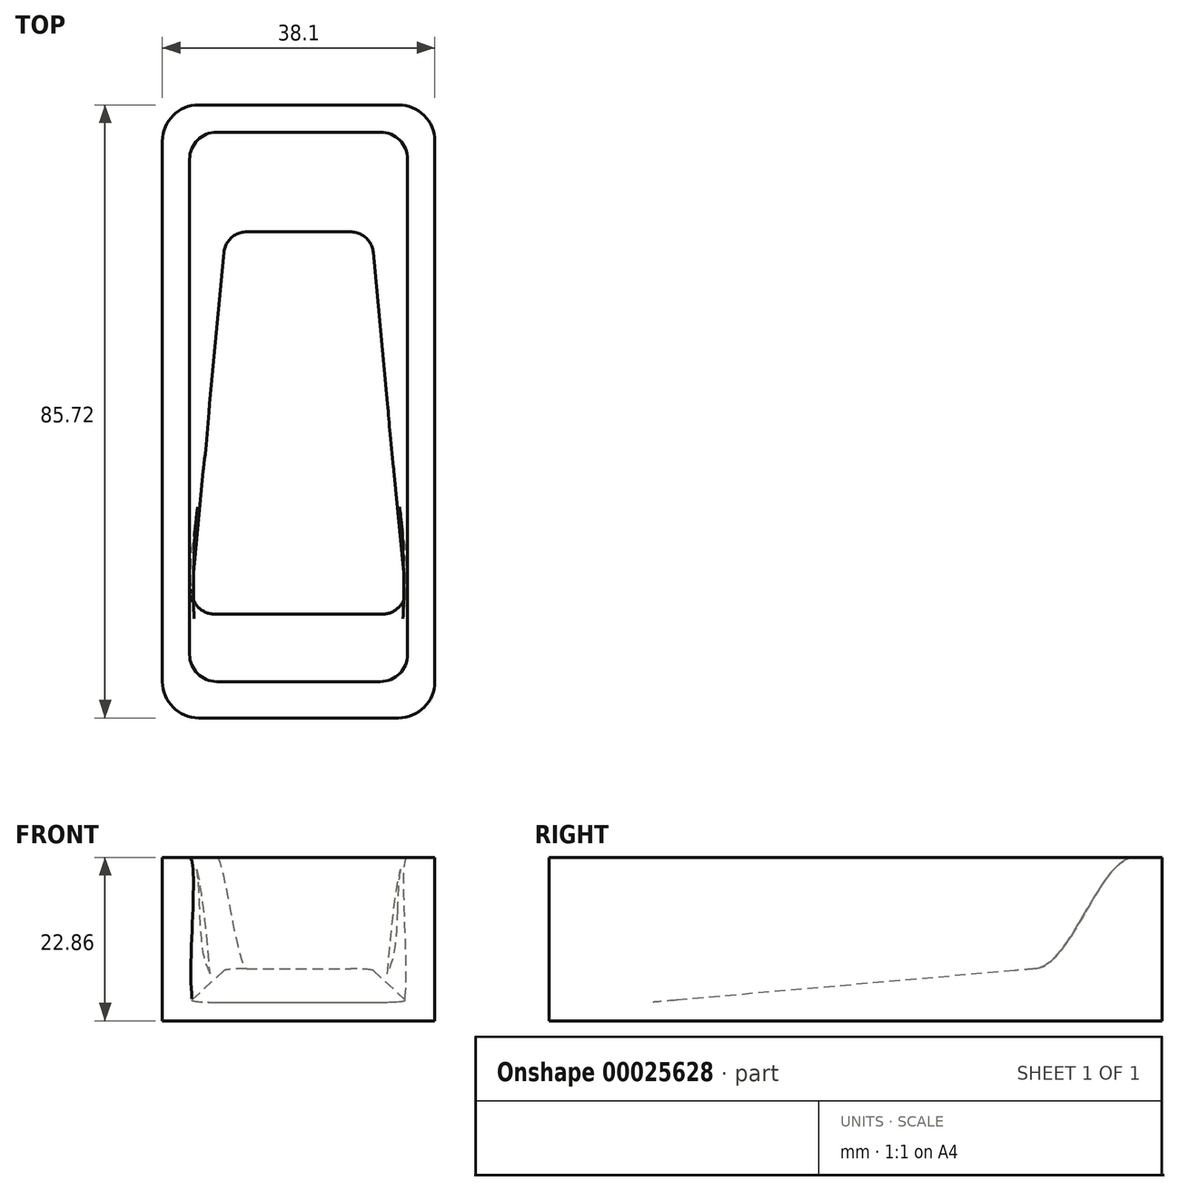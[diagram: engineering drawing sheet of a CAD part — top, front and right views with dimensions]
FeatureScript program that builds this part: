
annotation { "Feature Type Name" : "Feature", "Feature Type Description" : "" }
export const myFeature = defineFeature(function(context is Context, id is Id, definition is map)
    precondition{}
    {
        {
            var Q0;
            Q0=qCreatedBy(makeId("Top.planeOp"),FACE);
            var sketch = newSketch(context, id + "F0", { "sketchPlane" : qUnion([Q0])});
            skLineSegment(sketch, "E0.bottom", {"start": v(-19.05, 42.86) * mm, "end": v(19.05, 42.86) * mm});
            skLineSegment(sketch, "E0.top", {"start": v(-19.05, -42.86) * mm, "end": v(19.05, -42.86) * mm});
            skLineSegment(sketch, "E0.left", {"start": v(-19.05, 42.86) * mm, "end": v(-19.05, -42.86) * mm});
            skLineSegment(sketch, "E0.right", {"start": v(19.05, 42.86) * mm, "end": v(19.05, -42.86) * mm});
            skSolve(sketch);
        }
        {
            var Q0;
            Q0 = qSketchRegion(id + "F0", true);
            extrude(context, id + "F1", {"entities" : qUnion([Q0]), "depth" : 22.86 * mm});
        }
        {
            var Q0;
            Q0=qCreatedBy(makeId("Top.planeOp"),FACE);
            cPlane(context, id + "F2", {"entities" : qUnion([Q0]), "cplaneType" : CPlaneType.OFFSET, "offset" : 5.08 * mm, "width" : 152.4 * mm, "height" : 152.4 * mm});
        }
        {
            var Q0;
            Q0=qCreatedBy(id+"F2.planeOp",FACE);
            var sketch = newSketch(context, id + "F3", { "sketchPlane" : qUnion([Q0])});
            skLineSegment(sketch, "E1", {"start": v(-38.1, 0) * mm, "end": v(38.1, 0) * mm, "construction": true});
            skSolve(sketch);
        }
        {
            var Q0;
            Q0=sQuery(id+"F3.wireOp",EDGE,"E1");
            cPlane(context, id + "F4", {"entities" : qUnion([Q0]), "cplaneType" : CPlaneType.LINE_ANGLE, "offset" : 152.4 * mm, "angle" : 95 * degree, "width" : 152.4 * mm, "height" : 152.4 * mm});
        }
        {
            var Q0;
            Q0=makeQuery(id+"F1.opExtrude","CAP_FACE",FACE,{"disambiguationData":[OSD([sQuery(id+"F0.wireOp",EDGE,"E0.bottom"),sQuery(id+"F0.wireOp",EDGE,"E0.top"),sQuery(id+"F0.wireOp",EDGE,"E0.left"),sQuery(id+"F0.wireOp",EDGE,"E0.right")])],"isStart":false});
            var sketch = newSketch(context, id + "F5", { "sketchPlane" : qUnion([Q0])});
            skLineSegment(sketch, "E2.bottom", {"start": v(-11.43, 39.05) * mm, "end": v(11.43, 39.05) * mm});
            skLineSegment(sketch, "E2.top", {"start": v(-11.43, -37.78) * mm, "end": v(11.43, -37.78) * mm});
            skLineSegment(sketch, "E2.left", {"start": v(-15.24, 35.24) * mm, "end": v(-15.24, -33.97) * mm});
            skLineSegment(sketch, "E2.right", {"start": v(15.24, 35.24) * mm, "end": v(15.24, -33.97) * mm});
            skPoint(sketch, "E3.visualSharp", {"position": v(-15.24, 39.05) * mm});
            skArc(sketch, "E3.filletArc", {"start": v(-11.43, 39.05) * mm, "mid": v(-14.12, 37.94) * mm, "end": v(-15.24, 35.24) * mm});
            skPoint(sketch, "E4.visualSharp", {"position": v(15.24, 39.05) * mm});
            skArc(sketch, "E4.filletArc", {"start": v(15.24, 35.24) * mm, "mid": v(14.12, 37.94) * mm, "end": v(11.43, 39.05) * mm});
            skPoint(sketch, "E5.visualSharp", {"position": v(15.24, -37.78) * mm});
            skArc(sketch, "E5.filletArc", {"start": v(11.43, -37.78) * mm, "mid": v(14.12, -36.67) * mm, "end": v(15.24, -33.97) * mm});
            skPoint(sketch, "E6.visualSharp", {"position": v(-15.24, -37.78) * mm});
            skArc(sketch, "E6.filletArc", {"start": v(-15.24, -33.97) * mm, "mid": v(-14.12, -36.67) * mm, "end": v(-11.43, -37.78) * mm});
            skSolve(sketch);
        }
        {
            var Q0;
            Q0=qCreatedBy(id+"F4.planeOp",FACE);
            var sketch = newSketch(context, id + "F6", { "sketchPlane" : qUnion([Q0])});
            skLineSegment(sketch, "E7.bottom", {"start": v(-7.27, 25.64) * mm, "end": v(7.27, 25.64) * mm});
            skLineSegment(sketch, "E7.top", {"start": v(-11.75, -28) * mm, "end": v(11.75, -28) * mm});
            skLineSegment(sketch, "E7.left", {"start": v(-10.43, 22.77) * mm, "end": v(-14.91, -24.53) * mm});
            skLineSegment(sketch, "E7.right", {"start": v(10.43, 22.77) * mm, "end": v(14.91, -24.53) * mm});
            skPoint(sketch, "E8.visualSharp", {"position": v(-10.16, 25.64) * mm});
            skArc(sketch, "E8.filletArc", {"start": v(-7.27, 25.64) * mm, "mid": v(-9.4, 24.82) * mm, "end": v(-10.43, 22.77) * mm});
            skPoint(sketch, "E9.visualSharp", {"position": v(10.16, 25.64) * mm});
            skArc(sketch, "E9.filletArc", {"start": v(10.43, 22.77) * mm, "mid": v(9.4, 24.82) * mm, "end": v(7.27, 25.64) * mm});
            skPoint(sketch, "E10.visualSharp", {"position": v(15.24, -28) * mm});
            skArc(sketch, "E10.filletArc", {"start": v(11.75, -28) * mm, "mid": v(14.1, -26.97) * mm, "end": v(14.91, -24.53) * mm});
            skPoint(sketch, "E11.visualSharp", {"position": v(-15.24, -28) * mm});
            skArc(sketch, "E11.filletArc", {"start": v(-14.91, -24.53) * mm, "mid": v(-14.1, -26.97) * mm, "end": v(-11.75, -28) * mm});
            skSolve(sketch);
        }
        {
            var Q1;
            Q1 = qSketchRegion(id + "F5", true);
            var Q2;
            Q2 = qSketchRegion(id + "F6", true);
            loft(context, id + "F7", {"operationType" : NewBodyOperationType.REMOVE, "startCondition" : LoftEndDerivativeType.MATCH_TANGENT, "startMagnitude" : 1, "endCondition" : LoftEndDerivativeType.TANGENT_TO_PROFILE, "endMagnitude" : 1, "sheetProfilesArray" : [{ "sheetProfileEntities" : qUnion([Q1]) }, { "sheetProfileEntities" : qUnion([Q2]) }]});
        }
        {
            var Q0;
            Q0=makeQuery(id+"F1.opExtrude","SWEPT_EDGE",EDGE,{"disambiguationData":[OSD([sQuery(id+"F0.wireOp",EDGE,"E0.bottom"),sQuery(id+"F0.wireOp",EDGE,"E0.left")])]});
            var Q1;
            Q1=makeQuery(id+"F1.opExtrude","SWEPT_EDGE",EDGE,{"disambiguationData":[OSD([sQuery(id+"F0.wireOp",EDGE,"E0.top"),sQuery(id+"F0.wireOp",EDGE,"E0.left")])]});
            var Q2;
            Q2=makeQuery(id+"F1.opExtrude","SWEPT_EDGE",EDGE,{"disambiguationData":[OSD([sQuery(id+"F0.wireOp",EDGE,"E0.top"),sQuery(id+"F0.wireOp",EDGE,"E0.right")])]});
            var Q3;
            Q3=makeQuery(id+"F1.opExtrude","SWEPT_EDGE",EDGE,{"disambiguationData":[OSD([sQuery(id+"F0.wireOp",EDGE,"E0.bottom"),sQuery(id+"F0.wireOp",EDGE,"E0.right")])]});
            fillet(context, id + "F8", {"entities" : qUnion([Q0, Q1, Q2, Q3]), "radius" : 5.08 * mm, "tangentPropagation" : true, "allowEdgeOverflow" : false});
        }
    });
